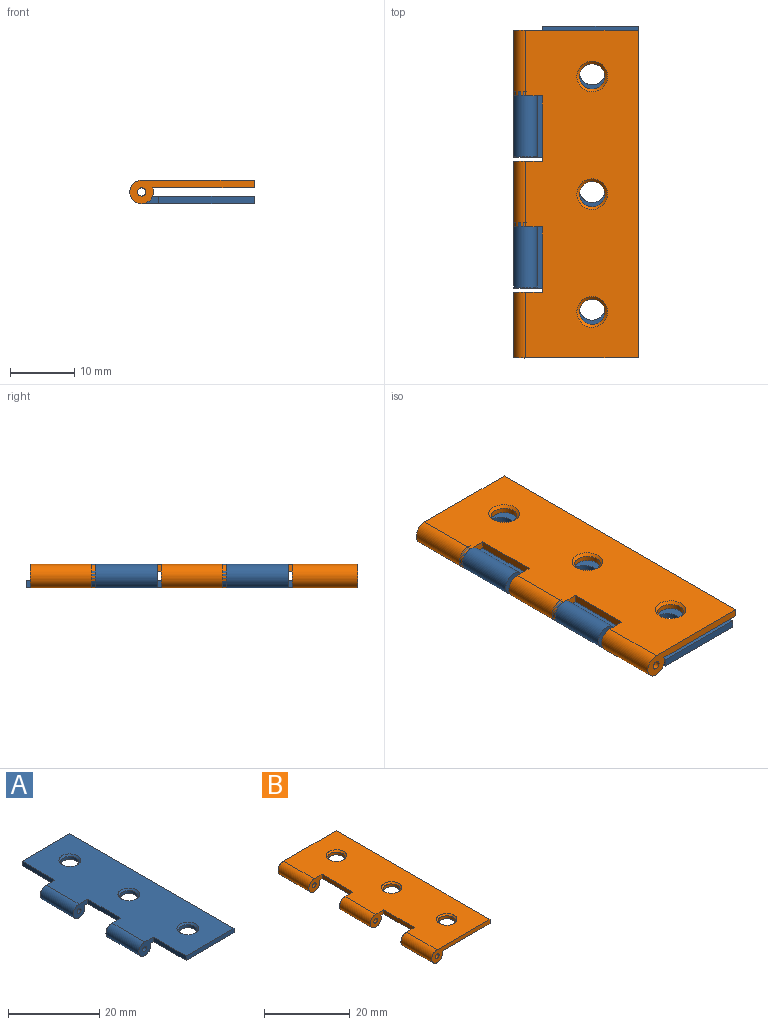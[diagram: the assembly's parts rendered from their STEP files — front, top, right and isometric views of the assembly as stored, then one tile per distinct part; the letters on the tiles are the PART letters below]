
ASSEMBLY  parts=2 mates=1
PART A: 22 faces, bbox 19.3x50.8x3.7 mm
  f0: plane 50.8x17.46mm, normal (0,0,1), area 752.4mm2, adj f1,f2,f4,f5,f6,f8,f10,f12
  f1: cylinder r=1.83mm len=10.16mm, axis (0,1,0), area 94mm2, adj f0,f3,f15,f19
  f2: cylinder r=1.83mm len=10.16mm, axis (0,1,0), area 94mm2, adj f0,f3,f13,f16
  f3: plane 50.8x15.75mm, normal (0,0,-1), area 733.9mm2, adj f1,f2,f4,f5,f6,f7,f9,f11
  f4: plane 50.8x1.19mm, normal (1,0,0), area 60.5mm2, adj f0,f3,f5,f6
  f5: plane 14.8x1.19mm, normal (0,-1,0), area 17.6mm2, adj f0,f3,f4,f14
  f6: plane 14.8x1.19mm, normal (0,1,0), area 17.6mm2, adj f0,f3,f4,f20
  f7: cylinder r=1.98mm len=3.97mm, axis (0,0,1), area 9.9mm2, adj f3,f8
  f8: cone r=1.98mm half-angle=45deg, axis (0,0,1), area 7.7mm2, adj f0,f7
  f9: cylinder r=1.98mm len=3.97mm, axis (0,0,1), area 9.9mm2, adj f3,f10
  f10: cone r=1.98mm half-angle=45deg, axis (0,0,1), area 7.7mm2, adj f0,f9
  f11: cylinder r=1.98mm len=3.97mm, axis (0,0,1), area 9.9mm2, adj f3,f12
  f12: cone r=1.98mm half-angle=45deg, axis (0,0,1), area 7.7mm2, adj f0,f11
  f13: plane 4.49x3.65mm, normal (0,-1,0), area 10.9mm2, adj f0,f2,f3,f14,f21
  f14: plane 10.16x1.19mm, normal (-1,0,0), area 12.1mm2, adj f0,f3,f5,f13
  f15: plane 4.49x3.65mm, normal (0,-1,0), area 10.9mm2, adj f0,f1,f3,f17,f18
  f16: plane 4.49x3.65mm, normal (0,1,0), area 10.9mm2, adj f0,f2,f3,f17,f21
  f17: plane 10.16x1.19mm, normal (-1,0,0), area 12.1mm2, adj f0,f3,f15,f16
  f18: cylinder r=0.64mm len=10.16mm, axis (0,1,0), area 40.5mm2, adj f15,f19
  f19: plane 4.49x3.65mm, normal (0,1,0), area 10.9mm2, adj f0,f1,f3,f18,f20
  f20: plane 10.16x1.19mm, normal (-1,0,0), area 12.1mm2, adj f0,f3,f6,f19
  f21: cylinder r=0.64mm len=10.16mm, axis (0,1,0), area 40.5mm2, adj f13,f16
PART B: 23 faces, bbox 19.3x50.8x3.7 mm
  f0: plane 50.8x17.46mm, normal (0,0,1), area 780.4mm2, adj f1,f2,f5,f6,f8,f9,f11,f13
  f1: cylinder r=1.83mm len=10.16mm, axis (0,1,0), area 94mm2, adj f0,f3,f9,f20
  f2: cylinder r=1.83mm len=10.16mm, axis (0,1,0), area 94mm2, adj f0,f3,f16,f21
  f3: plane 50.8x15.75mm, normal (0,0,-1), area 744.6mm2, adj f1,f2,f5,f6,f8,f9,f10,f12
  f4: cylinder r=0.64mm len=10.16mm, axis (0,1,0), area 40.5mm2, adj f9,f20
  f5: plane 50.8x1.19mm, normal (1,0,0), area 60.5mm2, adj f0,f3,f8,f9
  f6: cylinder r=1.83mm len=10.16mm, axis (0,1,0), area 94mm2, adj f0,f3,f8,f17
  f7: cylinder r=0.64mm len=10.16mm, axis (0,1,0), area 40.5mm2, adj f8,f17
  f8: plane 19.29x3.65mm, normal (0,-1,0), area 28.5mm2, adj f0,f3,f5,f6,f7
  f9: plane 19.29x3.65mm, normal (0,1,0), area 28.5mm2, adj f0,f1,f3,f4,f5
  f10: cylinder r=1.98mm len=3.97mm, axis (0,0,1), area 9.9mm2, adj f3,f11
  f11: cone r=1.98mm half-angle=45deg, axis (0,0,1), area 7.7mm2, adj f0,f10
  f12: cylinder r=1.98mm len=3.97mm, axis (0,0,1), area 9.9mm2, adj f3,f13
  f13: cone r=1.98mm half-angle=45deg, axis (0,0,1), area 7.7mm2, adj f0,f12
  f14: cylinder r=1.98mm len=3.97mm, axis (0,0,1), area 9.9mm2, adj f3,f15
  f15: cone r=1.98mm half-angle=45deg, axis (0,0,1), area 7.7mm2, adj f0,f14
  f16: plane 4.45x3.65mm, normal (0,-1,0), area 10.8mm2, adj f0,f2,f3,f18,f19
  f17: plane 4.45x3.65mm, normal (0,1,0), area 10.8mm2, adj f0,f3,f6,f7,f18
  f18: plane 10.16x1.19mm, normal (-1,0,0), area 12.1mm2, adj f0,f3,f16,f17
  f19: cylinder r=0.64mm len=10.16mm, axis (0,1,0), area 40.5mm2, adj f16,f21
  f20: plane 4.45x3.65mm, normal (0,-1,0), area 10.8mm2, adj f0,f1,f3,f4,f22
  f21: plane 4.45x3.65mm, normal (0,1,0), area 10.8mm2, adj f0,f2,f3,f19,f22
  f22: plane 10.16x1.19mm, normal (-1,0,0), area 12.1mm2, adj f0,f3,f20,f21
PLACE A rot(axis=(1,0,0),180deg) t=(0.2,-5.74,-12.68)mm
PLACE B rot(axis=(-0.35,-0.87,-0.35),0deg) t=(0.2,44.37,-9.02)mm
MATE cylindrical A.f18 <-> B.f4  axis (0,-1,0) through (0.2,24.74,-10.85)mm
